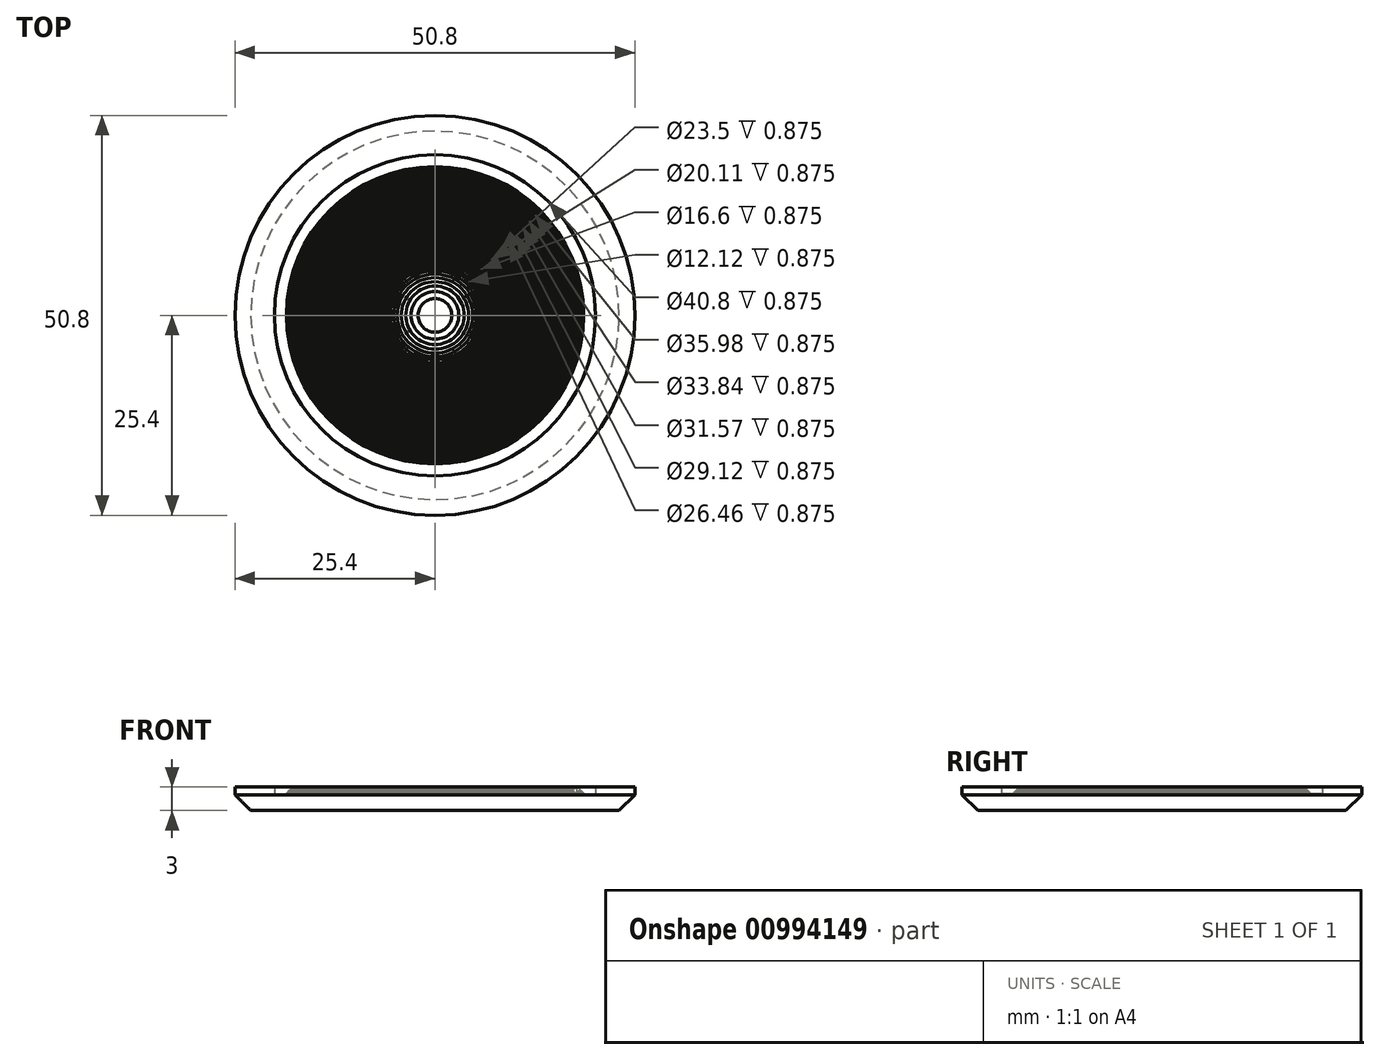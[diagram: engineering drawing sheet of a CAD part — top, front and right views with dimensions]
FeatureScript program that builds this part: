
annotation { "Feature Type Name" : "Feature", "Feature Type Description" : "" }
export const myFeature = defineFeature(function(context is Context, id is Id, definition is map)
    precondition{}
    {
        {
            var Q0;
            Q0=qCreatedBy(makeId("Front.planeOp"),FACE);
            var sketch = newSketch(context, id + "F0", { "sketchPlane" : qUnion([Q0])});
            skLineSegment(sketch, "E0", {"start": v(-10.56, 1.5) * mm, "end": v(-12.7, 1.5) * mm});
            skLineSegment(sketch, "E1", {"start": v(-10.56, 1.37) * mm, "end": v(-10.56, 1.5) * mm});
            skLineSegment(sketch, "E2", {"start": v(-9.67, 1.25) * mm, "end": v(-9.67, 1.37) * mm});
            skLineSegment(sketch, "E3", {"start": v(-9.67, 1.37) * mm, "end": v(-10.56, 1.37) * mm});
            skLineSegment(sketch, "E4", {"start": v(-8.99, 1.12) * mm, "end": v(-8.99, 1.25) * mm});
            skLineSegment(sketch, "E5", {"start": v(-8.99, 1.25) * mm, "end": v(-9.67, 1.25) * mm});
            skLineSegment(sketch, "E6", {"start": v(-8.42, 1) * mm, "end": v(-8.42, 1.12) * mm});
            skLineSegment(sketch, "E7", {"start": v(-8.42, 1.12) * mm, "end": v(-8.99, 1.12) * mm});
            skLineSegment(sketch, "E8", {"start": v(-7.9, 0.87) * mm, "end": v(-7.9, 1) * mm});
            skLineSegment(sketch, "E9", {"start": v(-7.9, 1) * mm, "end": v(-8.42, 1) * mm});
            skLineSegment(sketch, "E10", {"start": v(-7.45, 0.75) * mm, "end": v(-7.45, 0.87) * mm});
            skLineSegment(sketch, "E11", {"start": v(-7.45, 0.87) * mm, "end": v(-7.9, 0.87) * mm});
            skLineSegment(sketch, "E12", {"start": v(-7.03, 0.62) * mm, "end": v(-7.03, 0.75) * mm});
            skLineSegment(sketch, "E13", {"start": v(-7.03, 0.75) * mm, "end": v(-7.45, 0.75) * mm});
            skLineSegment(sketch, "E14", {"start": v(-6.64, 0.62) * mm, "end": v(-7.03, 0.62) * mm});
            skLineSegment(sketch, "E15", {"start": v(-6.27, 1.37) * mm, "end": v(-6.27, 1.5) * mm});
            skLineSegment(sketch, "E16", {"start": v(-6.64, 0.62) * mm, "end": v(-6.64, 1.5) * mm});
            skLineSegment(sketch, "E17", {"start": v(-6.64, 1.5) * mm, "end": v(-6.27, 1.5) * mm});
            skLineSegment(sketch, "E18", {"start": v(-5.92, 1.25) * mm, "end": v(-5.92, 1.37) * mm});
            skLineSegment(sketch, "E19", {"start": v(-5.92, 1.37) * mm, "end": v(-6.27, 1.37) * mm});
            skLineSegment(sketch, "E20", {"start": v(-5.6, 1.12) * mm, "end": v(-5.6, 1.25) * mm});
            skLineSegment(sketch, "E21", {"start": v(-5.6, 1.25) * mm, "end": v(-5.92, 1.25) * mm});
            skLineSegment(sketch, "E22", {"start": v(-5.28, 1) * mm, "end": v(-5.28, 1.12) * mm});
            skLineSegment(sketch, "E23", {"start": v(-5.28, 1.12) * mm, "end": v(-5.6, 1.12) * mm});
            skLineSegment(sketch, "E24", {"start": v(-4.97, 0.87) * mm, "end": v(-4.97, 1) * mm});
            skLineSegment(sketch, "E25", {"start": v(-4.97, 1) * mm, "end": v(-5.28, 1) * mm});
            skLineSegment(sketch, "E26", {"start": v(-4.68, 0.62) * mm, "end": v(-4.68, 0.87) * mm});
            skLineSegment(sketch, "E27", {"start": v(-4.68, 0.87) * mm, "end": v(-4.97, 0.87) * mm});
            skLineSegment(sketch, "E28", {"start": v(-4.4, 0.62) * mm, "end": v(-4.68, 0.62) * mm});
            skLineSegment(sketch, "E29", {"start": v(-4.4, 0.62) * mm, "end": v(-4.4, 1.5) * mm});
            skLineSegment(sketch, "E30", {"start": v(-4.13, 1.37) * mm, "end": v(-4.13, 1.5) * mm});
            skLineSegment(sketch, "E31", {"start": v(-4.13, 1.5) * mm, "end": v(-4.4, 1.5) * mm});
            skLineSegment(sketch, "E32", {"start": v(-3.86, 1.25) * mm, "end": v(-3.86, 1.37) * mm});
            skLineSegment(sketch, "E33", {"start": v(-3.86, 1.37) * mm, "end": v(-4.13, 1.37) * mm});
            skLineSegment(sketch, "E34", {"start": v(-3.6, 1.12) * mm, "end": v(-3.6, 1.25) * mm});
            skLineSegment(sketch, "E35", {"start": v(-3.6, 1.25) * mm, "end": v(-3.86, 1.25) * mm});
            skLineSegment(sketch, "E36", {"start": v(-3.35, 1) * mm, "end": v(-3.35, 1.12) * mm});
            skLineSegment(sketch, "E37", {"start": v(-3.35, 1.12) * mm, "end": v(-3.6, 1.12) * mm});
            skLineSegment(sketch, "E38", {"start": v(-3.11, 0.87) * mm, "end": v(-3.11, 1) * mm});
            skLineSegment(sketch, "E39", {"start": v(-3.11, 1) * mm, "end": v(-3.35, 1) * mm});
            skLineSegment(sketch, "E40", {"start": v(-2.88, 0.62) * mm, "end": v(-2.88, 0.87) * mm});
            skLineSegment(sketch, "E41", {"start": v(-2.88, 0.87) * mm, "end": v(-3.11, 0.87) * mm});
            skLineSegment(sketch, "E42", {"start": v(-2.64, 0.62) * mm, "end": v(-2.88, 0.62) * mm});
            skLineSegment(sketch, "E43", {"start": v(-2.42, 1.37) * mm, "end": v(-2.42, 1.5) * mm});
            skLineSegment(sketch, "E44", {"start": v(-2.64, 0.62) * mm, "end": v(-2.64, 1.5) * mm});
            skLineSegment(sketch, "E45", {"start": v(-2.64, 1.5) * mm, "end": v(-2.42, 1.5) * mm});
            skLineSegment(sketch, "E46", {"start": v(-2.2, 1.25) * mm, "end": v(-2.2, 1.37) * mm});
            skLineSegment(sketch, "E47", {"start": v(-2.2, 1.37) * mm, "end": v(-2.42, 1.37) * mm});
            skLineSegment(sketch, "E48", {"start": v(-1.98, 1.12) * mm, "end": v(-1.98, 1.25) * mm});
            skLineSegment(sketch, "E49", {"start": v(-1.98, 1.25) * mm, "end": v(-2.2, 1.25) * mm});
            skLineSegment(sketch, "E50", {"start": v(-1.76, 1) * mm, "end": v(-1.76, 1.12) * mm});
            skLineSegment(sketch, "E51", {"start": v(-1.76, 1.12) * mm, "end": v(-1.98, 1.12) * mm});
            skLineSegment(sketch, "E52", {"start": v(-1.55, 0.87) * mm, "end": v(-1.55, 1) * mm});
            skLineSegment(sketch, "E53", {"start": v(-1.55, 1) * mm, "end": v(-1.76, 1) * mm});
            skLineSegment(sketch, "E54", {"start": v(-1.35, 0.75) * mm, "end": v(-1.35, 0.87) * mm});
            skLineSegment(sketch, "E55", {"start": v(-1.35, 0.87) * mm, "end": v(-1.55, 0.87) * mm});
            skLineSegment(sketch, "E56", {"start": v(-1.15, 0.62) * mm, "end": v(-1.15, 0.75) * mm});
            skLineSegment(sketch, "E57", {"start": v(-1.15, 0.75) * mm, "end": v(-1.35, 0.75) * mm});
            skLineSegment(sketch, "E58", {"start": v(-0.95, 0.62) * mm, "end": v(-1.15, 0.62) * mm});
            skLineSegment(sketch, "E59", {"start": v(-0.76, 1.37) * mm, "end": v(-0.76, 1.5) * mm});
            skLineSegment(sketch, "E60", {"start": v(-0.95, 0.62) * mm, "end": v(-0.95, 1.5) * mm});
            skLineSegment(sketch, "E61", {"start": v(-0.95, 1.5) * mm, "end": v(-0.76, 1.5) * mm});
            skLineSegment(sketch, "E62", {"start": v(-0.56, 1.25) * mm, "end": v(-0.56, 1.37) * mm});
            skLineSegment(sketch, "E63", {"start": v(-0.56, 1.37) * mm, "end": v(-0.76, 1.37) * mm});
            skLineSegment(sketch, "E64", {"start": v(-0.38, 1.12) * mm, "end": v(-0.38, 1.25) * mm});
            skLineSegment(sketch, "E65", {"start": v(-0.38, 1.25) * mm, "end": v(-0.56, 1.25) * mm});
            skLineSegment(sketch, "E66", {"start": v(-0.19, 1) * mm, "end": v(-0.19, 1.12) * mm});
            skLineSegment(sketch, "E67", {"start": v(-0.19, 1.12) * mm, "end": v(-0.38, 1.12) * mm});
            skLineSegment(sketch, "E68", {"start": v(0, 0.87) * mm, "end": v(0, 1) * mm});
            skLineSegment(sketch, "E69", {"start": v(0, 1) * mm, "end": v(-0.19, 1) * mm});
            skLineSegment(sketch, "E70", {"start": v(0.18, 0.75) * mm, "end": v(0.18, 0.87) * mm});
            skLineSegment(sketch, "E71", {"start": v(0.18, 0.87) * mm, "end": v(0, 0.87) * mm});
            skLineSegment(sketch, "E72", {"start": v(0.35, 0.62) * mm, "end": v(0.35, 0.75) * mm});
            skLineSegment(sketch, "E73", {"start": v(0.35, 0.75) * mm, "end": v(0.18, 0.75) * mm});
            skLineSegment(sketch, "E74", {"start": v(0.53, 0.62) * mm, "end": v(0.35, 0.62) * mm});
            skLineSegment(sketch, "E75", {"start": v(0.53, 0.62) * mm, "end": v(0.53, 1.5) * mm});
            skLineSegment(sketch, "E76", {"start": v(0.7, 1.37) * mm, "end": v(0.7, 1.5) * mm});
            skLineSegment(sketch, "E77", {"start": v(0.7, 1.5) * mm, "end": v(0.53, 1.5) * mm});
            skLineSegment(sketch, "E78", {"start": v(0.88, 1.25) * mm, "end": v(0.88, 1.37) * mm});
            skLineSegment(sketch, "E79", {"start": v(0.88, 1.37) * mm, "end": v(0.7, 1.37) * mm});
            skLineSegment(sketch, "E80", {"start": v(1.04, 1.12) * mm, "end": v(1.04, 1.25) * mm});
            skLineSegment(sketch, "E81", {"start": v(1.04, 1.25) * mm, "end": v(0.88, 1.25) * mm});
            skLineSegment(sketch, "E82", {"start": v(1.21, 1) * mm, "end": v(1.21, 1.12) * mm});
            skLineSegment(sketch, "E83", {"start": v(1.21, 1.12) * mm, "end": v(1.04, 1.12) * mm});
            skLineSegment(sketch, "E84", {"start": v(1.38, 0.87) * mm, "end": v(1.38, 1) * mm});
            skLineSegment(sketch, "E85", {"start": v(1.38, 1) * mm, "end": v(1.21, 1) * mm});
            skLineSegment(sketch, "E86", {"start": v(1.54, 0.75) * mm, "end": v(1.54, 0.87) * mm});
            skLineSegment(sketch, "E87", {"start": v(1.54, 0.87) * mm, "end": v(1.38, 0.87) * mm});
            skLineSegment(sketch, "E88", {"start": v(1.7, 0.62) * mm, "end": v(1.7, 0.75) * mm});
            skLineSegment(sketch, "E89", {"start": v(1.7, 0.75) * mm, "end": v(1.54, 0.75) * mm});
            skLineSegment(sketch, "E90", {"start": v(1.86, 0.62) * mm, "end": v(1.7, 0.62) * mm});
            skLineSegment(sketch, "E91", {"start": v(2.02, 1.37) * mm, "end": v(2.02, 1.5) * mm});
            skLineSegment(sketch, "E92", {"start": v(1.86, 0.62) * mm, "end": v(1.86, 1.5) * mm});
            skLineSegment(sketch, "E93", {"start": v(1.86, 1.5) * mm, "end": v(2.02, 1.5) * mm});
            skLineSegment(sketch, "E94", {"start": v(2.18, 1.25) * mm, "end": v(2.18, 1.37) * mm});
            skLineSegment(sketch, "E95", {"start": v(2.18, 1.37) * mm, "end": v(2.02, 1.37) * mm});
            skLineSegment(sketch, "E96", {"start": v(2.33, 1.12) * mm, "end": v(2.33, 1.25) * mm});
            skLineSegment(sketch, "E97", {"start": v(2.33, 1.25) * mm, "end": v(2.18, 1.25) * mm});
            skLineSegment(sketch, "E98", {"start": v(2.49, 1) * mm, "end": v(2.49, 1.12) * mm});
            skLineSegment(sketch, "E99", {"start": v(2.49, 1.12) * mm, "end": v(2.33, 1.12) * mm});
            skLineSegment(sketch, "E100", {"start": v(2.64, 0.87) * mm, "end": v(2.64, 1) * mm});
            skLineSegment(sketch, "E101", {"start": v(2.64, 1) * mm, "end": v(2.49, 1) * mm});
            skLineSegment(sketch, "E102", {"start": v(2.79, 0.75) * mm, "end": v(2.79, 0.87) * mm});
            skLineSegment(sketch, "E103", {"start": v(2.79, 0.87) * mm, "end": v(2.64, 0.87) * mm});
            skLineSegment(sketch, "E104", {"start": v(2.94, 0.62) * mm, "end": v(2.94, 0.75) * mm});
            skLineSegment(sketch, "E105", {"start": v(2.94, 0.75) * mm, "end": v(2.79, 0.75) * mm});
            skLineSegment(sketch, "E106", {"start": v(3.08, 0.62) * mm, "end": v(2.94, 0.62) * mm});
            skLineSegment(sketch, "E107", {"start": v(3.08, 0.62) * mm, "end": v(3.08, 1.5) * mm});
            skLineSegment(sketch, "E108", {"start": v(3.23, 1.37) * mm, "end": v(3.23, 1.5) * mm});
            skLineSegment(sketch, "E109", {"start": v(3.23, 1.5) * mm, "end": v(3.08, 1.5) * mm});
            skLineSegment(sketch, "E110", {"start": v(3.38, 1.25) * mm, "end": v(3.38, 1.37) * mm});
            skLineSegment(sketch, "E111", {"start": v(3.38, 1.37) * mm, "end": v(3.23, 1.37) * mm});
            skLineSegment(sketch, "E112", {"start": v(3.52, 1.12) * mm, "end": v(3.52, 1.25) * mm});
            skLineSegment(sketch, "E113", {"start": v(3.52, 1.25) * mm, "end": v(3.38, 1.25) * mm});
            skLineSegment(sketch, "E114", {"start": v(3.66, 1) * mm, "end": v(3.66, 1.12) * mm});
            skLineSegment(sketch, "E115", {"start": v(3.66, 1.12) * mm, "end": v(3.52, 1.12) * mm});
            skLineSegment(sketch, "E116", {"start": v(3.8, 0.87) * mm, "end": v(3.8, 1) * mm});
            skLineSegment(sketch, "E117", {"start": v(3.8, 1) * mm, "end": v(3.66, 1) * mm});
            skLineSegment(sketch, "E118", {"start": v(3.95, 0.75) * mm, "end": v(3.95, 0.87) * mm});
            skLineSegment(sketch, "E119", {"start": v(3.95, 0.87) * mm, "end": v(3.8, 0.87) * mm});
            skLineSegment(sketch, "E120", {"start": v(4.08, 0.62) * mm, "end": v(4.08, 0.75) * mm});
            skLineSegment(sketch, "E121", {"start": v(4.08, 0.75) * mm, "end": v(3.95, 0.75) * mm});
            skLineSegment(sketch, "E122", {"start": v(4.22, 0.62) * mm, "end": v(4.08, 0.62) * mm});
            skLineSegment(sketch, "E123", {"start": v(4.22, 0.62) * mm, "end": v(4.22, 1.5) * mm});
            skLineSegment(sketch, "E124", {"start": v(4.36, 1.37) * mm, "end": v(4.36, 1.5) * mm});
            skLineSegment(sketch, "E125", {"start": v(4.36, 1.5) * mm, "end": v(4.22, 1.5) * mm});
            skLineSegment(sketch, "E126", {"start": v(4.5, 1.25) * mm, "end": v(4.5, 1.37) * mm});
            skLineSegment(sketch, "E127", {"start": v(4.5, 1.37) * mm, "end": v(4.36, 1.37) * mm});
            skLineSegment(sketch, "E128", {"start": v(4.63, 1.12) * mm, "end": v(4.63, 1.25) * mm});
            skLineSegment(sketch, "E129", {"start": v(4.63, 1.25) * mm, "end": v(4.5, 1.25) * mm});
            skLineSegment(sketch, "E130", {"start": v(4.76, 1) * mm, "end": v(4.76, 1.12) * mm});
            skLineSegment(sketch, "E131", {"start": v(4.76, 1.12) * mm, "end": v(4.63, 1.12) * mm});
            skLineSegment(sketch, "E132", {"start": v(4.9, 0.87) * mm, "end": v(4.9, 1) * mm});
            skLineSegment(sketch, "E133", {"start": v(4.9, 1) * mm, "end": v(4.76, 1) * mm});
            skLineSegment(sketch, "E134", {"start": v(5.03, 0.75) * mm, "end": v(5.03, 0.87) * mm});
            skLineSegment(sketch, "E135", {"start": v(5.03, 0.87) * mm, "end": v(4.9, 0.87) * mm});
            skLineSegment(sketch, "E136", {"start": v(5.16, 0.62) * mm, "end": v(5.16, 0.75) * mm});
            skLineSegment(sketch, "E137", {"start": v(5.16, 0.75) * mm, "end": v(5.03, 0.75) * mm});
            skLineSegment(sketch, "E138", {"start": v(5.29, 0.62) * mm, "end": v(5.16, 0.62) * mm});
            skLineSegment(sketch, "E139", {"start": v(5.29, 0.62) * mm, "end": v(5.29, 1.5) * mm});
            skLineSegment(sketch, "E140", {"start": v(5.42, 1.37) * mm, "end": v(5.42, 1.5) * mm});
            skLineSegment(sketch, "E141", {"start": v(5.42, 1.5) * mm, "end": v(5.29, 1.5) * mm});
            skLineSegment(sketch, "E142", {"start": v(5.55, 1.25) * mm, "end": v(5.55, 1.37) * mm});
            skLineSegment(sketch, "E143", {"start": v(5.55, 1.37) * mm, "end": v(5.42, 1.37) * mm});
            skLineSegment(sketch, "E144", {"start": v(5.67, 1.12) * mm, "end": v(5.67, 1.25) * mm});
            skLineSegment(sketch, "E145", {"start": v(5.67, 1.25) * mm, "end": v(5.55, 1.25) * mm});
            skLineSegment(sketch, "E146", {"start": v(5.8, 1) * mm, "end": v(5.8, 1.12) * mm});
            skLineSegment(sketch, "E147", {"start": v(5.8, 1.12) * mm, "end": v(5.67, 1.12) * mm});
            skLineSegment(sketch, "E148", {"start": v(5.93, 0.87) * mm, "end": v(5.93, 1) * mm});
            skLineSegment(sketch, "E149", {"start": v(5.93, 1) * mm, "end": v(5.8, 1) * mm});
            skLineSegment(sketch, "E150", {"start": v(6.05, 0.75) * mm, "end": v(6.05, 0.87) * mm});
            skLineSegment(sketch, "E151", {"start": v(6.05, 0.87) * mm, "end": v(5.93, 0.87) * mm});
            skLineSegment(sketch, "E152", {"start": v(6.17, 0.62) * mm, "end": v(6.17, 0.75) * mm});
            skLineSegment(sketch, "E153", {"start": v(6.17, 0.75) * mm, "end": v(6.05, 0.75) * mm});
            skLineSegment(sketch, "E154", {"start": v(12.7, -1.5) * mm, "end": v(12.7, 1.5) * mm});
            skLineSegment(sketch, "E155", {"start": v(12.7, 1.5) * mm, "end": v(7.7, 1.5) * mm});
            skLineSegment(sketch, "E156", {"start": v(7.7, 1.5) * mm, "end": v(7.7, 0.62) * mm});
            skLineSegment(sketch, "E157", {"start": v(7.7, 0.62) * mm, "end": v(6.17, 0.62) * mm});
            skLineSegment(sketch, "E158", {"start": v(-12.7, -1.5) * mm, "end": v(12.7, -1.5) * mm});
            skLineSegment(sketch, "E159", {"start": v(-12.7, -1.5) * mm, "end": v(-12.7, 1.5) * mm});
            skSolve(sketch);
        }
        {
            var Q0;
            Q0=makeQuery(id+"F0.imprint","IMPRINT",FACE,{"disambiguationData":[TD([[makeQuery(id+"F0.imprint","IMPRINT",EDGE,{"derivedFrom":sQuery(id+"F0.wireOp",EDGE,"E0")}),1.0]])]});
            var Q1;
            Q1=sQuery(id+"F0.wireOp",EDGE,"E159");
            revolve(context, id + "F1", {"surfaceOperationType" : NewSurfaceOperationType.NEW, "entities" : qUnion([Q0]), "axis" : qUnion([Q1]), "revolveType" : RevolveType.FULL});
        }
        {
            var Q0;
            Q0=makeQuery(id+"F1.opRevolve","SWEPT_EDGE",EDGE,{"disambiguationData":[OSD([sQuery(id+"F0.wireOp",EDGE,"E154"),sQuery(id+"F0.wireOp",EDGE,"E158")])]});
            chamfer(context, id + "F2", {"entities" : qUnion([Q0]), "width" : 2 * mm, "tangentPropagation" : true});
        }
    });
